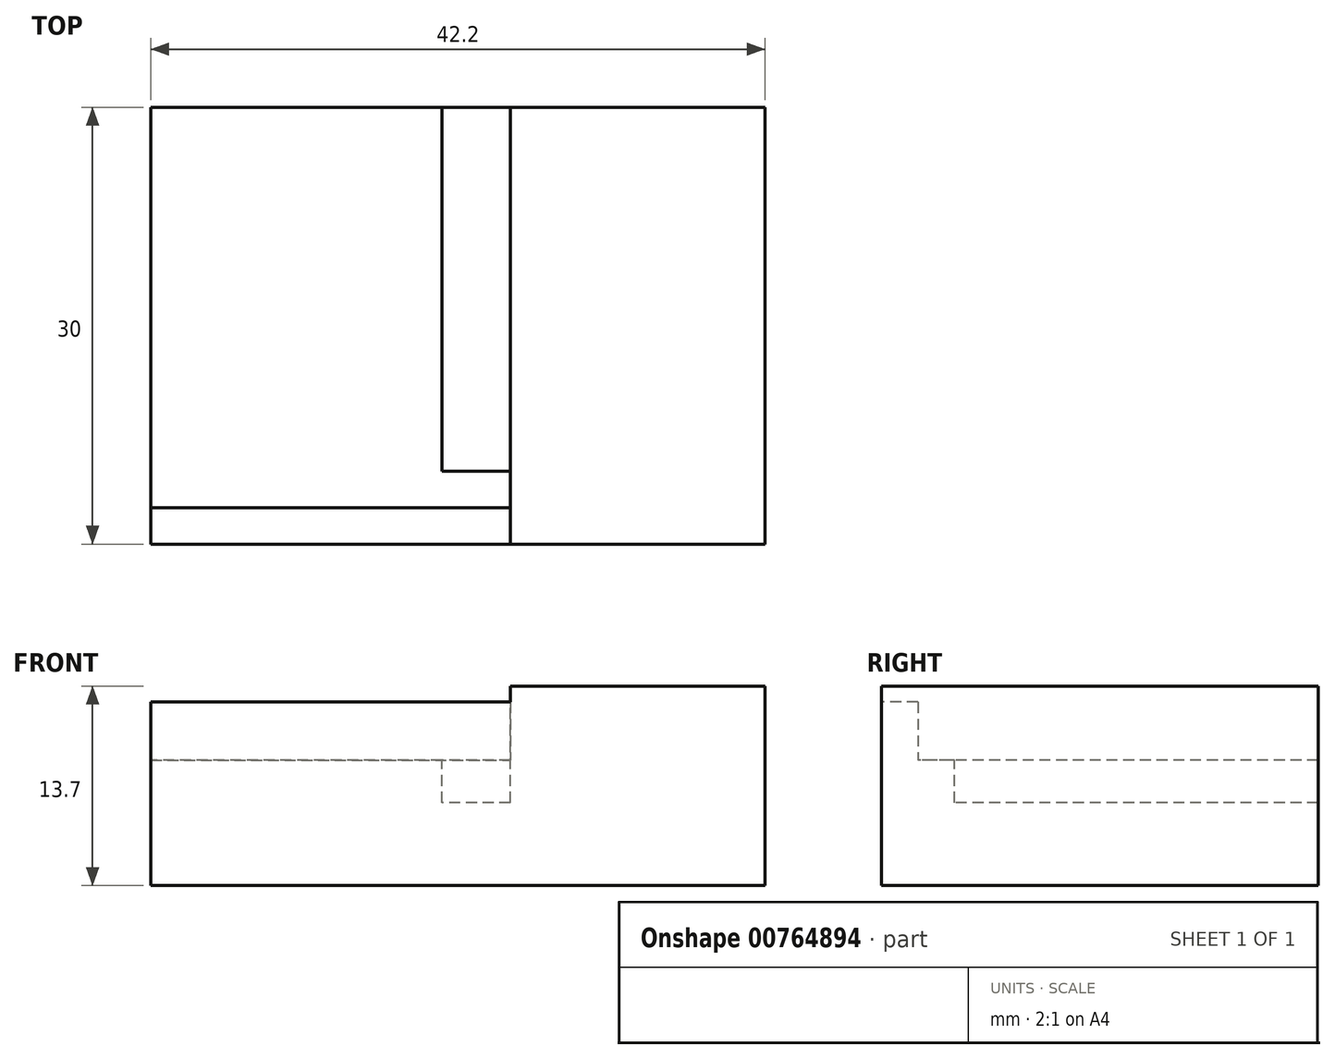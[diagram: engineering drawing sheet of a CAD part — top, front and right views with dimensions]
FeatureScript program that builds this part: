
annotation { "Feature Type Name" : "Feature", "Feature Type Description" : "" }
export const myFeature = defineFeature(function(context is Context, id is Id, definition is map)
    precondition{}
    {
        {
            var Q0;
            Q0=qCreatedBy(makeId("Front.planeOp"),FACE);
            var sketch = newSketch(context, id + "F0", { "sketchPlane" : qUnion([Q0])});
            skLineSegment(sketch, "E0.bottom", {"start": v(0, 0) * mm, "end": v(-42.2, 0) * mm});
            skLineSegment(sketch, "E0.top", {"start": v(0, 13.7) * mm, "end": v(-17.5, 13.7) * mm});
            skLineSegment(sketch, "E0.left", {"start": v(0, 0) * mm, "end": v(0, 13.7) * mm});
            skLineSegment(sketch, "E0.right", {"start": v(-42.2, 0) * mm, "end": v(-42.2, 8.6) * mm});
            skLineSegment(sketch, "E1.0", {"start": v(-17.5, 8.6) * mm, "end": v(-42.2, 8.6) * mm});
            skLineSegment(sketch, "E2.0", {"start": v(-22.2, 5.7) * mm, "end": v(-22.2, 8.6) * mm});
            skLineSegment(sketch, "E3.0", {"start": v(-17.5, 5.7) * mm, "end": v(-17.5, 13.7) * mm});
            skLineSegment(sketch, "E4.0", {"start": v(-17.5, 5.7) * mm, "end": v(-22.2, 5.7) * mm});
            skSolve(sketch);
        }
        {
            var Q0;
            Q0=makeQuery(id+"F0.imprint","IMPRINT",FACE,{"disambiguationData":[TD([[makeQuery(id+"F0.imprint","IMPRINT",EDGE,{"derivedFrom":sQuery(id+"F0.wireOp",EDGE,"E0.bottom")}),-1.0]])]});
            extrude(context, id + "F1", {"entities" : qUnion([Q0]), "oppositeDirection" : true, "depth" : 30 * mm, "offsetDistance" : 25 * mm});
        }
        {
            var Q0;
            {var subQ3=sQuery(id+"F0.wireOp",EDGE,"E2.0");Q0=makeQuery(id+"F0.imprint","IMPRINT",FACE,{"disambiguationData":[TD([[makeQuery(id+"F0.imprint","IMPRINT",EDGE,{"derivedFrom":subQ3}),-1.0]])]});}
            extrude(context, id + "F2", {"entities" : qUnion([Q0]), "operationType" : NewBodyOperationType.ADD, "oppositeDirection" : true, "depth" : 5 * mm, "offsetDistance" : 25 * mm});
        }
        {
            var Q0;
            {var subQ0=sQuery(id+"F0.wireOp",EDGE,"E1.0");Q0=makeQuery(id+"F2.boolean.opBoolean","MERGE",FACE,{"derivedFrom":[makeQuery(id+"F1.opExtrude","SWEPT_FACE",FACE,{"disambiguationData":[OSD([subQ0])]}),makeQuery(id+"F2.opExtrude","SWEPT_FACE",FACE,{"disambiguationData":[OSD([subQ0])]})]});}
            var sketch = newSketch(context, id + "F3", { "sketchPlane" : qUnion([Q0])});
            skLineSegment(sketch, "E5.bottom", {"start": v(-42.2, 2.5) * mm, "end": v(-17.5, 2.5) * mm});
            skLineSegment(sketch, "E5.top", {"start": v(-42.2, 0) * mm, "end": v(-17.5, 0) * mm});
            skLineSegment(sketch, "E5.left", {"start": v(-42.2, 2.5) * mm, "end": v(-42.2, 0) * mm});
            skLineSegment(sketch, "E5.right", {"start": v(-17.5, 2.5) * mm, "end": v(-17.5, 0) * mm});
            skSolve(sketch);
        }
        {
            var Q0;
            Q0=makeQuery(id+"F3.imprint","IMPRINT",FACE,{"disambiguationData":[TD([[makeQuery(id+"F3.imprint","IMPRINT",EDGE,{"derivedFrom":sQuery(id+"F3.wireOp",EDGE,"E5.bottom")}),-1.0]])]});
            extrude(context, id + "F4", {"entities" : qUnion([Q0]), "operationType" : NewBodyOperationType.ADD, "depth" : 4 * mm, "offsetDistance" : 25 * mm});
        }
    });
